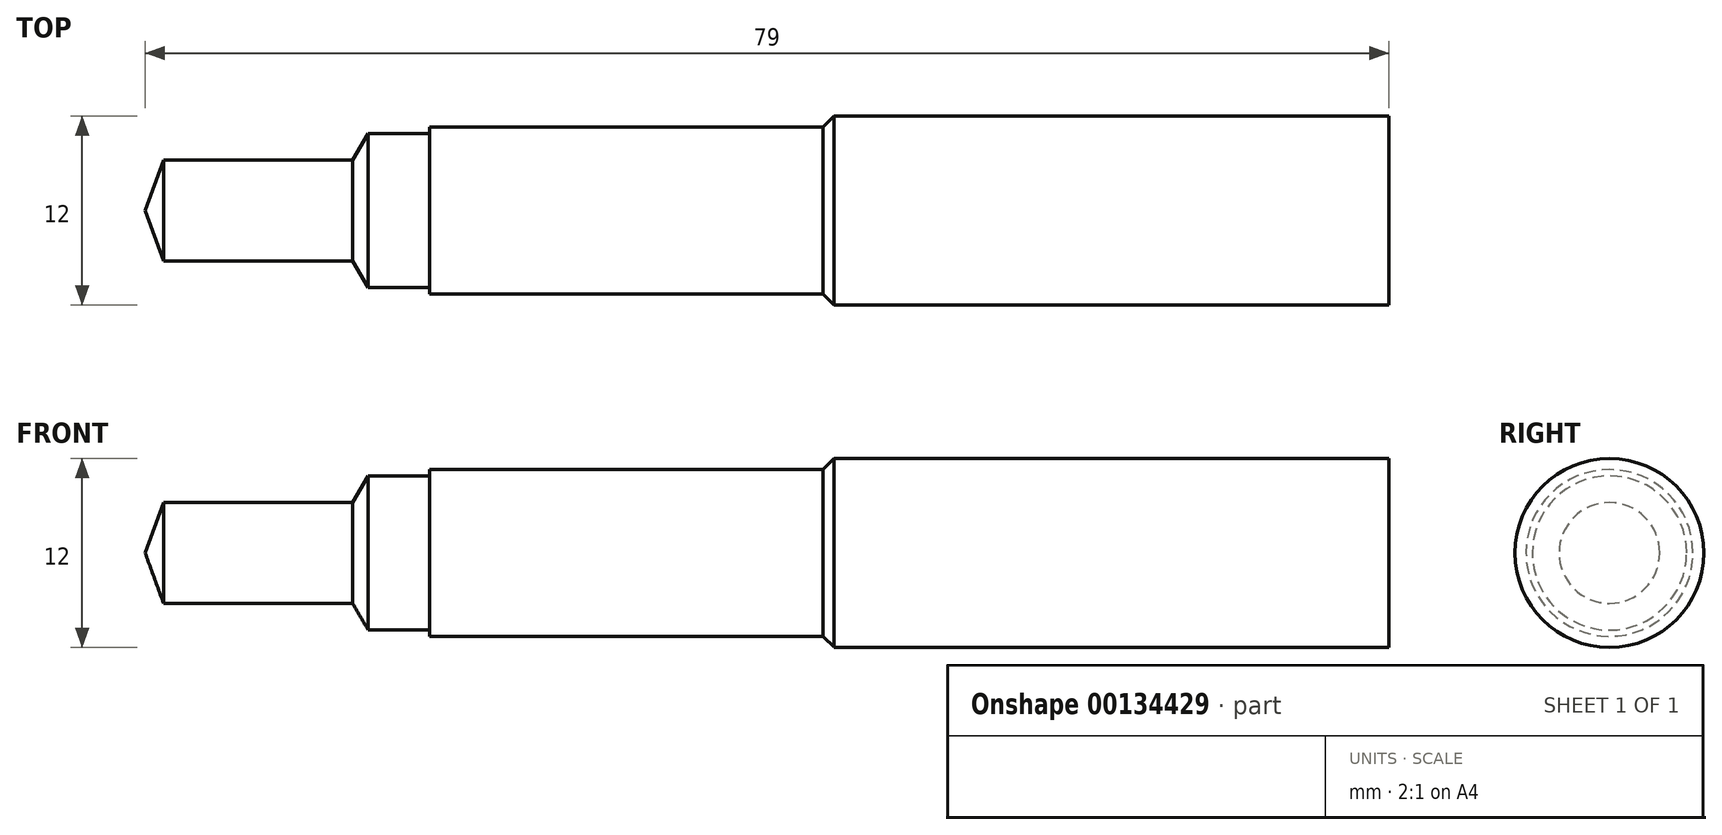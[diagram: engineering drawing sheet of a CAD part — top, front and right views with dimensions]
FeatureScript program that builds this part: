
annotation { "Feature Type Name" : "Feature", "Feature Type Description" : "" }
export const myFeature = defineFeature(function(context is Context, id is Id, definition is map)
    precondition{}
    {
        {
            var Q0;
            Q0=qCreatedBy(makeId("Front.planeOp"),FACE);
            var sketch = newSketch(context, id + "F0", { "sketchPlane" : qUnion([Q0])});
            skLineSegment(sketch, "E0", {"start": v(0, 0) * mm, "end": v(65.58, 0) * mm});
            skLineSegment(sketch, "E1", {"start": v(0, 0) * mm, "end": v(1.16, 3.2) * mm});
            skLineSegment(sketch, "E2", {"start": v(1.16, 3.2) * mm, "end": v(13.16, 3.2) * mm});
            skLineSegment(sketch, "E3", {"start": v(13.16, 3.2) * mm, "end": v(14.16, 4.9) * mm});
            skLineSegment(sketch, "E4", {"start": v(14.16, 4.9) * mm, "end": v(18.06, 4.9) * mm});
            skLineSegment(sketch, "E5", {"start": v(18.06, 4.9) * mm, "end": v(18.06, 5.3) * mm});
            skLineSegment(sketch, "E6", {"start": v(18.06, 5.3) * mm, "end": v(43.06, 5.3) * mm});
            skLineSegment(sketch, "E7", {"start": v(43.06, 5.3) * mm, "end": v(43.76, 6) * mm});
            skLineSegment(sketch, "E8", {"start": v(43.76, 6) * mm, "end": v(79, 6) * mm});
            skLineSegment(sketch, "E9", {"start": v(79, 6) * mm, "end": v(79, 0) * mm});
            skLineSegment(sketch, "E10", {"start": v(79, 0) * mm, "end": v(0, 0) * mm});
            skSolve(sketch);
        }
        {
            var Q0;
            {var subQ1=sQuery(id+"F0.wireOp",EDGE,"E1");Q0=makeQuery(id+"F0.imprint","IMPRINT",FACE,{"disambiguationData":[TD([[makeQuery(id+"F0.imprint","IMPRINT",EDGE,{"derivedFrom":subQ1}),-1.0]])]});}
            var Q1;
            Q1=sQuery(id+"F0.wireOp",EDGE,"E10");
            revolve(context, id + "F1", {"entities" : qUnion([Q0]), "axis" : qUnion([Q1]), "revolveType" : RevolveType.FULL});
        }
    });
